# Revit family: 63_PHILIPS_LuxSpace Square_DN572B PSED-E RML
name_source: partatom
category: Lighting Fixtures
revit_build: Autodesk Revit 2017 (Build: 20160225_1515(x64)
units: mm (PartAtom-declared; Revit-internal decimal feet)

## family parameters
Cut with Voids When Loaded = No
Host = Face
Light Source = No
Part Type = Normal
Room Calculation Point = No
Round Connector Dimension = Use Diameter
Shared = No

## types (1)
- No IES Available
    Default Elevation = 2438 mm
    Description = LuxSpace Square
    Lamp = LED
    Light loss factor = 1
    Manufacturer = Philips
    Model = DN572B PSED-E RML
    Type Comments = Recessed
    URL = http://www.lighting.philips.com
    Voltage (V) = 230
    Wattage Comments = 37W
    body height = 121 mm  [stored 0.396982 ft]
    ceiling thickness = 57 mm
    installation space height = 150 mm
    length = 150 mm
    light source = 3 mm  [stored 0.00984252 ft]
    rim height = 0 mm  [stored 0 ft]
    width = 190 mm  [stored 0.62336 ft]
    width opening = 180 mm

note: [stored X ft] marks values corroborated as IEEE doubles in the binary element streams (Revit-internal decimal feet)

## geometry (parser evidence)
native form markers: Sweep x8
no freeform markers — native parametric forms only
